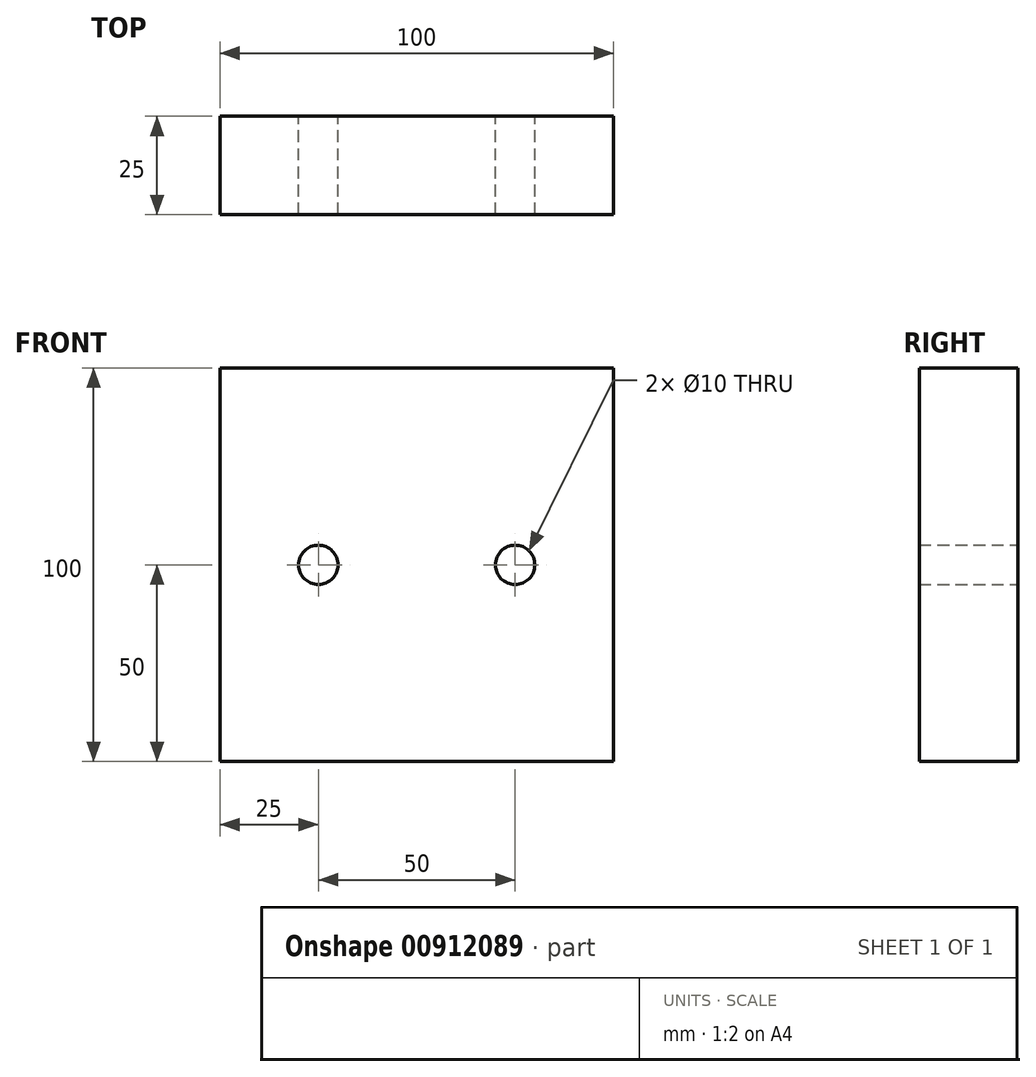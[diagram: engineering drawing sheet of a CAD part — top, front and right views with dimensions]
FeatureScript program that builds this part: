
annotation { "Feature Type Name" : "Feature", "Feature Type Description" : "" }
export const myFeature = defineFeature(function(context is Context, id is Id, definition is map)
    precondition{}
    {
        {
            var Q0;
            Q0=qCreatedBy(makeId("Front.planeOp"),FACE);
            var sketch = newSketch(context, id + "F0", { "sketchPlane" : qUnion([Q0])});
            skLineSegment(sketch, "E0.bottom", {"start": v(-50, 50) * mm, "end": v(50, 50) * mm});
            skLineSegment(sketch, "E0.top", {"start": v(-50, -50) * mm, "end": v(50, -50) * mm});
            skLineSegment(sketch, "E0.left", {"start": v(-50, 50) * mm, "end": v(-50, -50) * mm});
            skLineSegment(sketch, "E0.right", {"start": v(50, 50) * mm, "end": v(50, -50) * mm});
            skCircle(sketch, "E1", {"center": v(-25, 0) * mm, "radius": 5 * mm});
            skCircle(sketch, "E2", {"center": v(25, 0) * mm, "radius": 5 * mm});
            skSolve(sketch);
        }
        {
            var Q0;
            Q0=makeQuery(id+"F0.imprint","IMPRINT",FACE,{"disambiguationData":[TD([[makeQuery(id+"F0.imprint","IMPRINT",EDGE,{"derivedFrom":sQuery(id+"F0.wireOp",EDGE,"E0.bottom")}),-1.0]])]});
            extrude(context, id + "F1", {"entities" : qUnion([Q0]), "depth" : 25 * mm, "offsetDistance" : 25 * mm});
        }
    });
